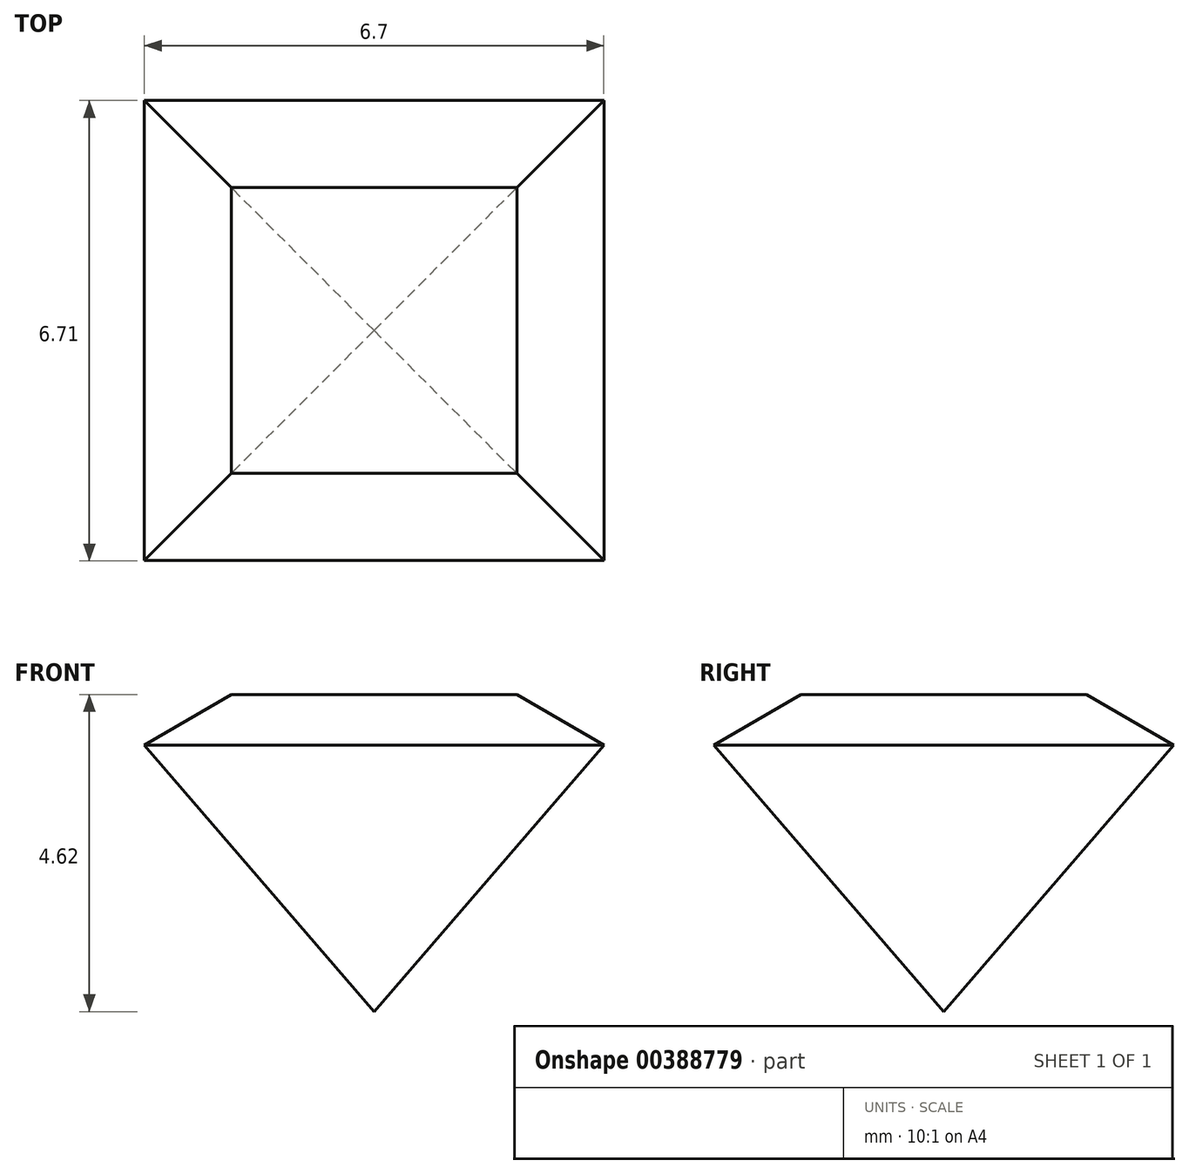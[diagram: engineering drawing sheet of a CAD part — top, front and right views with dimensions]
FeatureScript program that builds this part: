
annotation { "Feature Type Name" : "Feature", "Feature Type Description" : "" }
export const myFeature = defineFeature(function(context is Context, id is Id, definition is map)
    precondition{}
    {
        {
            var Q0;
            Q0=qCreatedBy(makeId("Front.planeOp"),FACE);
            var sketch = newSketch(context, id + "F0", { "sketchPlane" : qUnion([Q0])});
            skLineSegment(sketch, "E0", {"start": v(0, 0) * mm, "end": v(3.35, 0) * mm, "construction": true});
            skLineSegment(sketch, "E1", {"start": v(0, 0) * mm, "end": v(0, -4.62) * mm, "construction": true});
            skLineSegment(sketch, "E2", {"start": v(0, 0) * mm, "end": v(2.08, 0) * mm});
            skLineSegment(sketch, "E3", {"start": v(0, 0) * mm, "end": v(0, -0.74) * mm, "construction": true});
            skLineSegment(sketch, "E4", {"start": v(0, -0.74) * mm, "end": v(3.35, -0.74) * mm, "construction": true});
            skLineSegment(sketch, "E5", {"start": v(3.35, -0.74) * mm, "end": v(2.08, 0) * mm});
            skLineSegment(sketch, "E6", {"start": v(3.35, -0.74) * mm, "end": v(0, -4.62) * mm});
            skLineSegment(sketch, "E7.MirrorCS", {"start": v(0, 0) * mm, "end": v(-2.08, 0) * mm});
            skLineSegment(sketch, "E8.MirrorCS", {"start": v(-3.35, -0.74) * mm, "end": v(-2.08, 0) * mm});
            skLineSegment(sketch, "E9.MirrorCS", {"start": v(0, 0) * mm, "end": v(-3.35, 0) * mm, "construction": true});
            skLineSegment(sketch, "E10.MirrorCS", {"start": v(0, -0.74) * mm, "end": v(-3.35, -0.74) * mm, "construction": true});
            skLineSegment(sketch, "E11.MirrorCS", {"start": v(-3.35, -0.74) * mm, "end": v(0, -4.62) * mm});
            skSolve(sketch);
        }
        {
            var Q0;
            Q0 = qSketchRegion(id + "F0", true);
            extrude(context, id + "F1", {"entities" : qUnion([Q0]), "depth" : 6.7 * mm});
        }
        {
            var Q0;
            Q0=makeQuery(id+"F1.opExtrude","CAP_EDGE",EDGE,{"disambiguationData":[OSD([sQuery(id+"F0.wireOp",EDGE,"E2"),sQuery(id+"F0.wireOp",EDGE,"E7.MirrorCS")])],"isStart":false});
            var Q1;
            Q1=makeQuery(id+"F1.opExtrude","CAP_EDGE",EDGE,{"disambiguationData":[OSD([sQuery(id+"F0.wireOp",EDGE,"E2"),sQuery(id+"F0.wireOp",EDGE,"E7.MirrorCS")])],"isStart":true});
            chamfer(context, id + "F2", {"entities" : qUnion([Q0, Q1]), "chamferType" : ChamferType.TWO_OFFSETS, "width1" : 1.27 * mm, "oppositeDirection" : false, "width2" : 0.74 * mm, "tangentPropagation" : true});
        }
        {
            var Q0;
            Q0=qCreatedBy(makeId("Right.planeOp"),FACE);
            var sketch = newSketch(context, id + "F3", { "sketchPlane" : qUnion([Q0])});
            skLineSegment(sketch, "E12", {"start": v(0, 0) * mm, "end": v(-6.7, 0) * mm, "construction": true});
            skLineSegment(sketch, "E13", {"start": v(-6.7, 0) * mm, "end": v(-6.7, -0.74) * mm, "construction": true});
            skPoint(sketch, "E14", {"position": v(-3.35, 0) * mm});
            skLineSegment(sketch, "E15", {"start": v(0, 0) * mm, "end": v(0, -0.74) * mm, "construction": true});
            skLineSegment(sketch, "E16", {"start": v(-3.35, 0) * mm, "end": v(-3.35, -4.62) * mm, "construction": true});
            skLineSegment(sketch, "E17", {"start": v(-6.7, -0.74) * mm, "end": v(-3.35, -4.62) * mm});
            skLineSegment(sketch, "E18", {"start": v(0, -0.74) * mm, "end": v(-3.35, -4.62) * mm});
            skLineSegment(sketch, "E19", {"start": v(-6.7, -0.74) * mm, "end": v(-7.37, -5.01) * mm});
            skLineSegment(sketch, "E20", {"start": v(-7.37, -5.01) * mm, "end": v(0.52, -5.01) * mm});
            skLineSegment(sketch, "E21", {"start": v(0.52, -5.01) * mm, "end": v(0, -0.74) * mm});
            skSolve(sketch);
        }
        {
            var Q0;
            Q0 = qSketchRegion(id + "F3", true);
            extrude(context, id + "F4", {"entities" : qUnion([Q0]), "operationType" : NewBodyOperationType.REMOVE, "depth" : 25 * mm, "hasSecondDirection" : true, "secondDirectionOppositeDirection" : true, "secondDirectionDepth" : 25 * mm});
        }
    });
